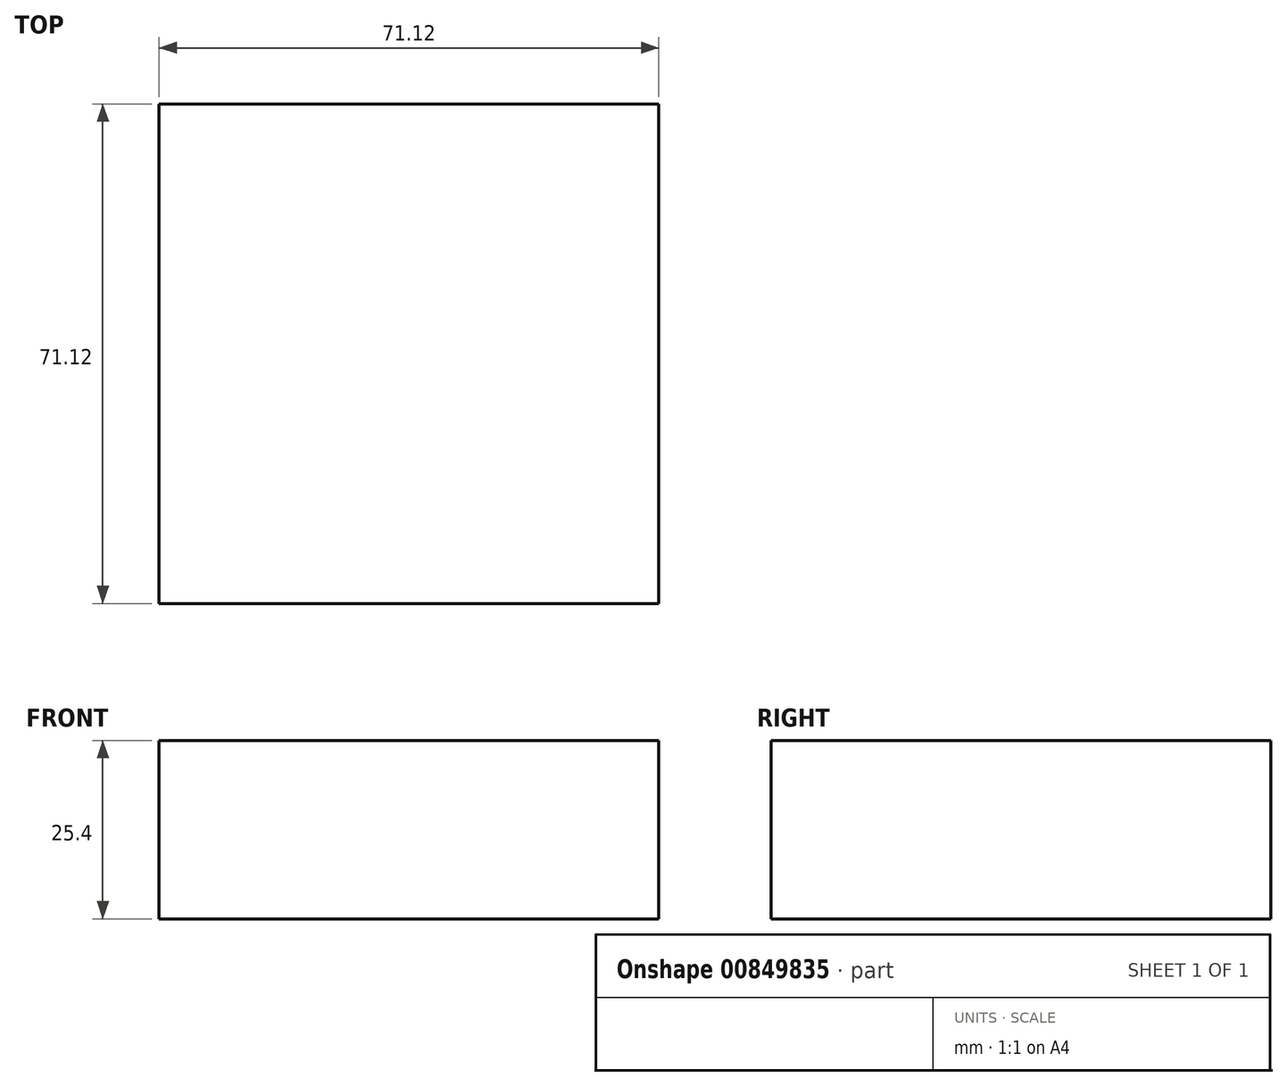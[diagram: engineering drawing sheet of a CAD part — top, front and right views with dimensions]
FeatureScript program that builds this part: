
annotation { "Feature Type Name" : "Feature", "Feature Type Description" : "" }
export const myFeature = defineFeature(function(context is Context, id is Id, definition is map)
    precondition{}
    {
        {
            var Q0;
            Q0=qCreatedBy(makeId("Top.planeOp"),FACE);
            var sketch = newSketch(context, id + "F0", { "sketchPlane" : qUnion([Q0])});
            skLineSegment(sketch, "E0.bottom", {"start": v(35.56, -35.56) * mm, "end": v(-35.56, -35.56) * mm});
            skLineSegment(sketch, "E0.top", {"start": v(35.56, 35.56) * mm, "end": v(-35.56, 35.56) * mm});
            skLineSegment(sketch, "E0.left", {"start": v(35.56, -35.56) * mm, "end": v(35.56, 35.56) * mm});
            skLineSegment(sketch, "E0.right", {"start": v(-35.56, -35.56) * mm, "end": v(-35.56, 35.56) * mm});
            skPoint(sketch, "E0.middle", {"position": v(0, 0) * mm});
            skSolve(sketch);
        }
        {
            var Q0;
            Q0=makeQuery(id+"F0.imprint","IMPRINT",FACE,{"disambiguationData":[TD([[makeQuery(id+"F0.imprint","IMPRINT",EDGE,{"derivedFrom":sQuery(id+"F0.wireOp",EDGE,"E0.bottom")}),-1.0]])]});
            extrude(context, id + "F1", {"entities" : qUnion([Q0]), "depth" : 25.4 * mm, "offsetDistance" : 25.4 * mm});
        }
    });
